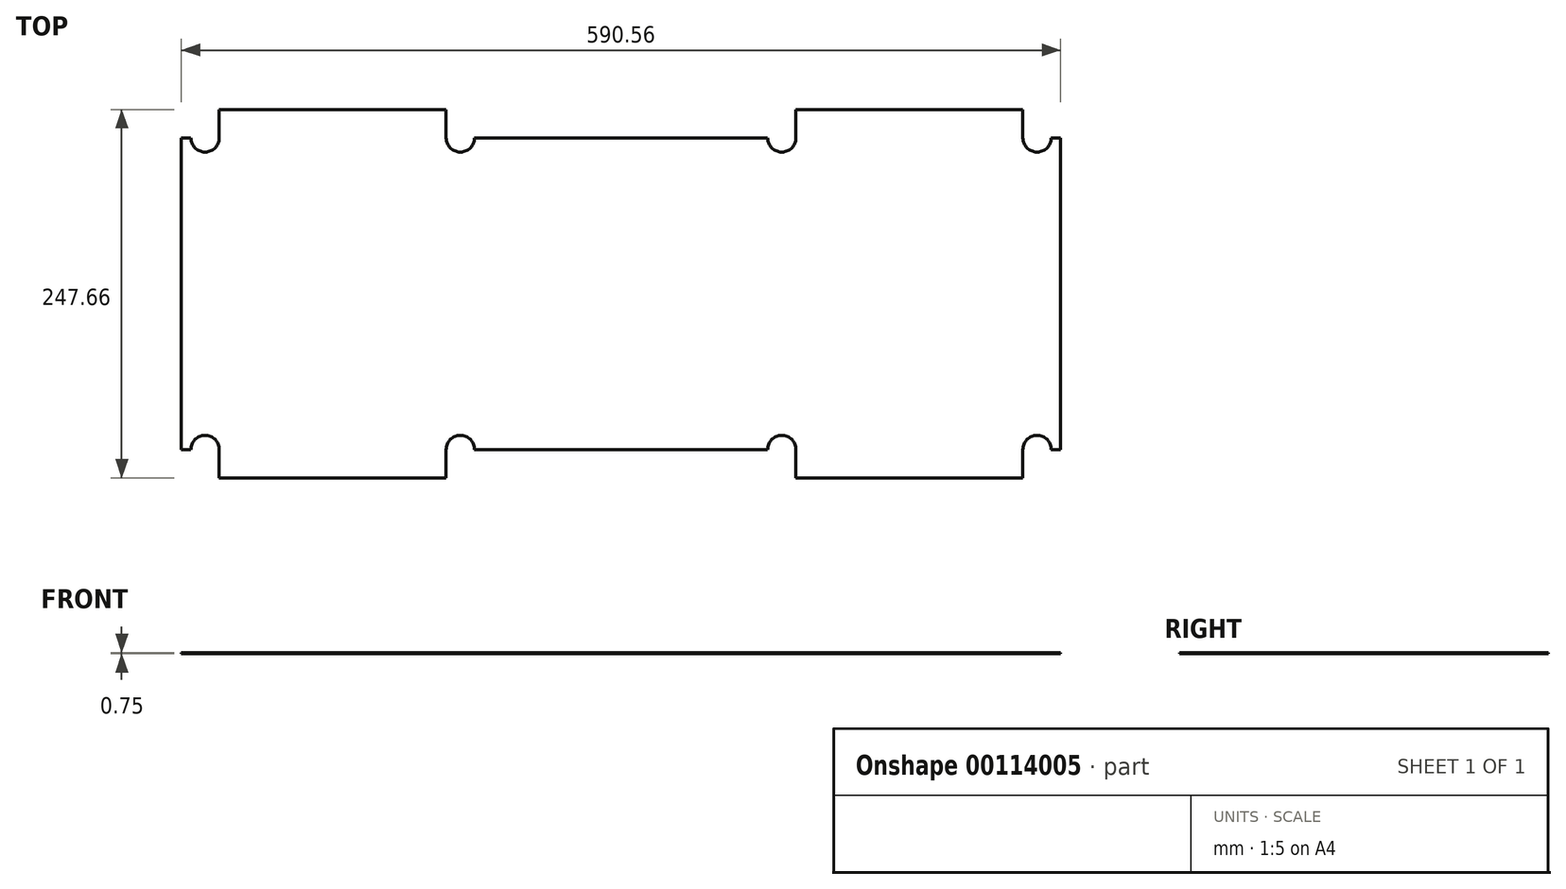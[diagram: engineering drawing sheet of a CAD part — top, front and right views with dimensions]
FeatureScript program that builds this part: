
annotation { "Feature Type Name" : "Feature", "Feature Type Description" : "" }
export const myFeature = defineFeature(function(context is Context, id is Id, definition is map)
    precondition{}
    {
        {
            assignVariable(context, id + "F0", {"name" : "thickness", "anyValue" : 3 / 4});
        }
        {
            var Q0;
            Q0=qCreatedBy(makeId("Top.planeOp"),FACE);
            var sketch = newSketch(context, id + "F1", { "sketchPlane" : qUnion([Q0])});
            skLineSegment(sketch, "E0.bottom", {"start": v(-295.28, 104.78) * mm, "end": v(295.28, 104.77) * mm});
            skLineSegment(sketch, "E0.top", {"start": v(-295.28, -104.77) * mm, "end": v(295.28, -104.78) * mm});
            skLineSegment(sketch, "E0.left", {"start": v(-295.28, 104.77) * mm, "end": v(-295.28, -104.77) * mm});
            skLineSegment(sketch, "E0.right", {"start": v(295.28, 104.77) * mm, "end": v(295.28, -104.77) * mm});
            skLineSegment(sketch, "E1", {"start": v(0, 0) * mm, "end": v(-295.28, 0) * mm, "construction": true});
            skPoint(sketch, "E2", {"position": v(-295.28, 0) * mm});
            skPoint(sketch, "E3", {"position": v(0, 104.78) * mm});
            skLineSegment(sketch, "E4", {"start": v(0, 0) * mm, "end": v(0, 104.78) * mm, "construction": true});
            skSolve(sketch);
        }
        {
            var Q0;
            Q0 = qSketchRegion(id + "F1", true);
            extrude(context, id + "F2", {"entities" : qUnion([Q0]), "depth" : (getVariable(context, 'thickness')) * mm});
        }
        {
            var Q0;
            Q0=makeQuery(id+"F2.opExtrude","CAP_FACE",FACE,{"disambiguationData":[OSD([sQuery(id+"F1.wireOp",EDGE,"E0.bottom"),sQuery(id+"F1.wireOp",EDGE,"E0.top"),sQuery(id+"F1.wireOp",EDGE,"E0.left"),sQuery(id+"F1.wireOp",EDGE,"E0.right")])],"isStart":false});
            var sketch = newSketch(context, id + "F3", { "sketchPlane" : qUnion([Q0])});
            skLineSegment(sketch, "E5.bottom", {"start": v(-269.88, 123.82) * mm, "end": v(-117.48, 123.82) * mm});
            skLineSegment(sketch, "E5.top", {"start": v(-269.88, -123.83) * mm, "end": v(-117.48, -123.83) * mm});
            skLineSegment(sketch, "E5.left", {"start": v(-269.88, 123.83) * mm, "end": v(-269.88, -123.83) * mm});
            skLineSegment(sketch, "E5.right", {"start": v(-117.48, 123.83) * mm, "end": v(-117.48, -123.83) * mm});
            skPoint(sketch, "E6", {"position": v(-269.88, 0) * mm});
            skLineSegment(sketch, "E7", {"start": v(0, 0) * mm, "end": v(-269.88, 0) * mm, "construction": true});
            skLineSegment(sketch, "E8", {"start": v(0, 76.05) * mm, "end": v(0, 0) * mm, "construction": true});
            skLineSegment(sketch, "E9.MirrorCS", {"start": v(269.88, 123.83) * mm, "end": v(269.88, -123.82) * mm});
            skLineSegment(sketch, "E10.MirrorCS", {"start": v(269.88, -123.83) * mm, "end": v(117.48, -123.83) * mm});
            skLineSegment(sketch, "E11.MirrorCS", {"start": v(269.88, 123.82) * mm, "end": v(117.48, 123.82) * mm});
            skLineSegment(sketch, "E12.MirrorCS", {"start": v(117.48, 123.83) * mm, "end": v(117.48, -123.82) * mm});
            skSolve(sketch);
        }
        {
            var Q0;
            Q0 = qSketchRegion(id + "F3", true);
            extrude(context, id + "F4", {"entities" : qUnion([Q0]), "operationType" : NewBodyOperationType.ADD, "oppositeDirection" : true, "depth" : (getVariable(context, 'thickness')) * mm});
        }
        {
            var Q0;
            Q0=makeQuery(id+"F4.boolean.opBoolean","MERGE",FACE,{"derivedFrom":[makeQuery(id+"F2.opExtrude","CAP_FACE",FACE,{"disambiguationData":[OSD([sQuery(id+"F1.wireOp",EDGE,"E0.bottom"),sQuery(id+"F1.wireOp",EDGE,"E0.top"),sQuery(id+"F1.wireOp",EDGE,"E0.left"),sQuery(id+"F1.wireOp",EDGE,"E0.right")])],"isStart":false}),makeQuery(id+"F4.opExtrude","CAP_FACE",FACE,{"disambiguationData":[OSD([sQuery(id+"F3.wireOp",EDGE,"E5.bottom"),sQuery(id+"F3.wireOp",EDGE,"E5.top"),sQuery(id+"F3.wireOp",EDGE,"E5.left"),sQuery(id+"F3.wireOp",EDGE,"E5.right")])],"isStart":true}),makeQuery(id+"F4.opExtrude","CAP_FACE",FACE,{"disambiguationData":[OSD([sQuery(id+"F3.wireOp",EDGE,"E9.MirrorCS"),sQuery(id+"F3.wireOp",EDGE,"E10.MirrorCS"),sQuery(id+"F3.wireOp",EDGE,"E11.MirrorCS"),sQuery(id+"F3.wireOp",EDGE,"E12.MirrorCS")])],"isStart":true})]});
            var sketch = newSketch(context, id + "F5", { "sketchPlane" : qUnion([Q0])});
            skArc(sketch, "E13", {"start": v(-117.48, 104.78) * mm, "mid": v(-107.95, 95.25) * mm, "end": v(-98.43, 104.78) * mm});
            skLineSegment(sketch, "E14", {"start": v(-117.48, 104.78) * mm, "end": v(-98.43, 104.78) * mm});
            skLineSegment(sketch, "E15", {"start": v(0, 0) * mm, "end": v(0, 38.58) * mm, "construction": true});
            skLineSegment(sketch, "E16", {"start": v(0, 0) * mm, "end": v(-30.76, 0) * mm, "construction": true});
            skArc(sketch, "E17.MirrorCS", {"start": v(-117.48, 104.78) * mm, "mid": v(-107.95, 114.3) * mm, "end": v(-98.43, 104.78) * mm});
            skLineSegment(sketch, "E18.MirrorCS", {"start": v(0, 209.55) * mm, "end": v(0, 170.97) * mm, "construction": true});
            skArc(sketch, "E19", {"start": v(-98.43, -104.77) * mm, "mid": v(-107.95, -95.25) * mm, "end": v(-117.48, -104.77) * mm});
            skArc(sketch, "E20", {"start": v(117.48, -104.78) * mm, "mid": v(107.95, -95.25) * mm, "end": v(98.43, -104.78) * mm});
            skArc(sketch, "E21", {"start": v(98.43, 104.77) * mm, "mid": v(107.95, 95.25) * mm, "end": v(117.48, 104.78) * mm});
            skLineSegment(sketch, "E22", {"start": v(98.43, 104.77) * mm, "end": v(117.48, 104.77) * mm});
            skLineSegment(sketch, "E23", {"start": v(117.48, -104.78) * mm, "end": v(98.43, -104.78) * mm});
            skLineSegment(sketch, "E24", {"start": v(-117.48, -104.78) * mm, "end": v(-98.43, -104.78) * mm});
            skArc(sketch, "E25", {"start": v(269.88, 104.77) * mm, "mid": v(279.4, 95.25) * mm, "end": v(288.93, 104.77) * mm});
            skLineSegment(sketch, "E26", {"start": v(269.88, 104.77) * mm, "end": v(288.93, 104.77) * mm});
            skArc(sketch, "E27", {"start": v(288.93, -104.78) * mm, "mid": v(279.4, -95.25) * mm, "end": v(269.88, -104.77) * mm});
            skArc(sketch, "E28", {"start": v(-269.88, -104.77) * mm, "mid": v(-279.4, -95.25) * mm, "end": v(-288.93, -104.77) * mm});
            skArc(sketch, "E29", {"start": v(-288.93, 104.78) * mm, "mid": v(-279.4, 95.25) * mm, "end": v(-269.88, 104.78) * mm});
            skLineSegment(sketch, "E30", {"start": v(-288.93, 104.78) * mm, "end": v(-269.88, 104.78) * mm});
            skLineSegment(sketch, "E31", {"start": v(-288.93, -104.77) * mm, "end": v(-269.88, -104.78) * mm});
            skLineSegment(sketch, "E32", {"start": v(288.93, -104.78) * mm, "end": v(269.88, -104.78) * mm});
            skSolve(sketch);
        }
        {
            var Q0;
            Q0 = qSketchRegion(id + "F5", true);
            extrude(context, id + "F6", {"entities" : qUnion([Q0]), "operationType" : NewBodyOperationType.REMOVE, "oppositeDirection" : true, "depth" : 25.4 * mm});
        }
    });
